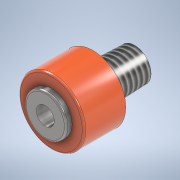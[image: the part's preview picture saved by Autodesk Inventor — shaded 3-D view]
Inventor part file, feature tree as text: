
AUTODESK INVENTOR PART (.ipt)
format: ipt  version: 2020 (Build 240168000, 168)  size: 165,376 bytes
history: native  units: mm
features: sketch x6, extrude x2, hole x2, fillet x2, plane x1, loft x1, thread x1
ambient origin geometry x8: Origin, YZ Plane, XZ Plane, XY Plane, X Axis, Y Axis, Z Axis, Center Point
bodies: Solid1 (feature_tree)
feature tree (15):
  extrude  "Extrusion1"  Depth=7.0mm TaperAngle=0.0deg
  extrude  "Extrusion2"  Depth=1.0mm TaperAngle=0.0deg
  hole  "Hole1"  [1 undecoded]
  fillet  "Fillet1"  Radius=0.3mm
  fillet  "Fillet2"  Radius=6.0mm
  sketch  "Sketch5"  dims[d8=3.0mm d9=6.0mm d10=4.0mm d11=2.0mm d12=90.0deg d13=8.0mm d14=20.594885mm d15=0.3mm d16=0.3mm d17=6.0mm]
  plane  "Work Plane1"
  loft  "Loft1"
  hole  "Hole2"  [1 undecoded]
  thread  "Thread1"  [1 undecoded]
  sketch  "Sketch1"  dims[d0=11.0mm d1=7.0mm d2=0.0mm]
  sketch  "Sketch2"  dims[d3=7.0mm d4=1.0mm d5=0.0mm]
  sketch  "Sketch4"  dims[d7=3.0mm]
  sketch  "Sketch6"  dims[d18=7.0mm d19=5.5mm]
  sketch  "Sketch7"  dims[d20=0.0mm d21=90.0deg d22=0.0mm d23=90.0deg d24=3.0mm d25=6.0mm d26=4.0mm d27=2.0mm d28=90.0deg d29=8.0mm d30=20.594885mm d31=9.0mm d32=0.0mm]
note: 3 required parameter values undecoded (feature->parameter linkage not recoverable at this tier; creation-order binding heuristic only, values carry confidence <= 0.55)
